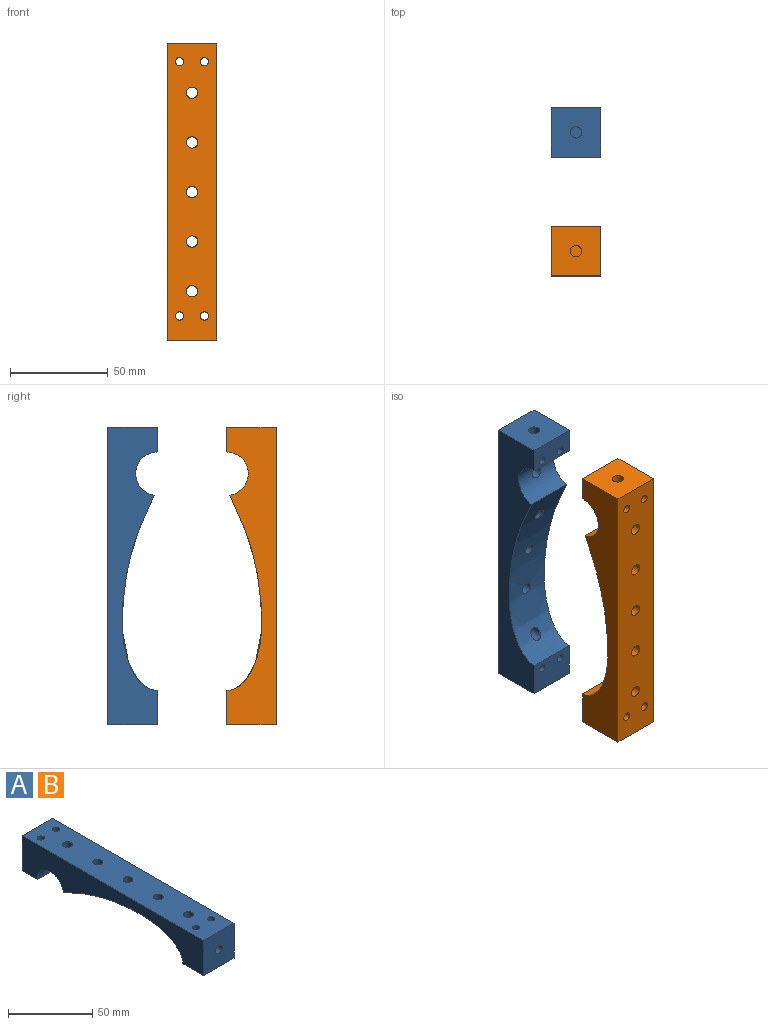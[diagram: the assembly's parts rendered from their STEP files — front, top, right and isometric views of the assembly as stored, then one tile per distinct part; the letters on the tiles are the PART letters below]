
ASSEMBLY  parts=2 mates=2
PART A: 22 faces, bbox 25.4x152.4x25.5 mm
  f0: plane 25.4x12.7mm, normal (0,0,-1), area 294.1mm2, adj f2,f3,f5,f8,f11,f12
  f1: extruded ~100.14x25.4mm, area 2693.5mm2, adj f2,f3,f4,f8,f18,f19,f20,f21
  f2: plane 152.4x25.49mm, normal (1,0,0), area 2356.7mm2, adj f0,f1,f4,f5,f6,f7,f8
  f3: plane 152.4x25.49mm, normal (-1,0,0), area 2357.1mm2, adj f0,f1,f4,f5,f6,f7,f8
  f4: plane 25.4x17.46mm, normal (0,0,-1), area 415.1mm2, adj f1,f2,f3,f6,f9,f10
  f5: plane 25.4x25.4mm, normal (0,1,0), area 618.4mm2, adj f0,f2,f3,f7,f15
  f6: plane 25.4x25.4mm, normal (0,-1,0), area 618.4mm2, adj f2,f3,f4,f7,f13
  f7: plane 152.4x25.4mm, normal (0,0,1), area 3680.1mm2, adj f2,f3,f5,f6,f9,f10,f11,f12
  f8: cylinder r=11.11mm len=25.4mm, axis (1,0,0), area 816.5mm2, adj f0,f1,f2,f3,f17
  f9: cylinder r=2.13mm len=25.4mm, axis (0,0,1), area 339.5mm2, adj f4,f7
  f10: cylinder r=2.13mm len=25.4mm, axis (0,0,1), area 339.5mm2, adj f4,f7
  f11: cylinder r=2.13mm len=25.4mm, axis (0,0,1), area 339.5mm2, adj f0,f7
  f12: cylinder r=2.13mm len=25.4mm, axis (0,0,1), area 339.5mm2, adj f0,f7
  f13: cylinder r=2.92mm len=12.7mm, axis (0,-1,0), area 233.1mm2, adj f6,f14
  f14: plane 5.84x5.84mm, normal (0,-1,0), area 26.8mm2, adj f13
  f15: cylinder r=2.92mm len=12.7mm, axis (0,1,0), area 233.1mm2, adj f5,f16
  f16: plane 5.84x5.84mm, normal (0,1,0), area 26.8mm2, adj f15
  f17: cylinder r=2.92mm len=15.24mm, axis (0,0,1), area 268mm2, adj f7,f8
  f18: cylinder r=2.92mm len=17.85mm, axis (0,0,1), area 306mm2, adj f1,f7
  f19: cylinder r=2.92mm len=10.03mm, axis (0,0,1), area 174.2mm2, adj f1,f7
  f20: cylinder r=2.92mm len=7.53mm, axis (0,0,1), area 136.1mm2, adj f1,f7
  f21: cylinder r=2.92mm len=16.06mm, axis (0,0,1), area 257mm2, adj f1,f7
PART B: same geometry as A
PLACE A rot(axis=(0,0.71,0.71),180deg) t=(0,35.42,19.05)mm
PLACE B rot(axis=(1,0,0),90deg) t=(-25.4,0,19.05)mm
MATE cylindrical B.f10 <-> A.f9  axis (0,1,0) through (-19.05,0,12.7)mm
MATE cylindrical B.f11 <-> A.f12  axis (0,1,0) through (-19.05,0,142.87)mm
